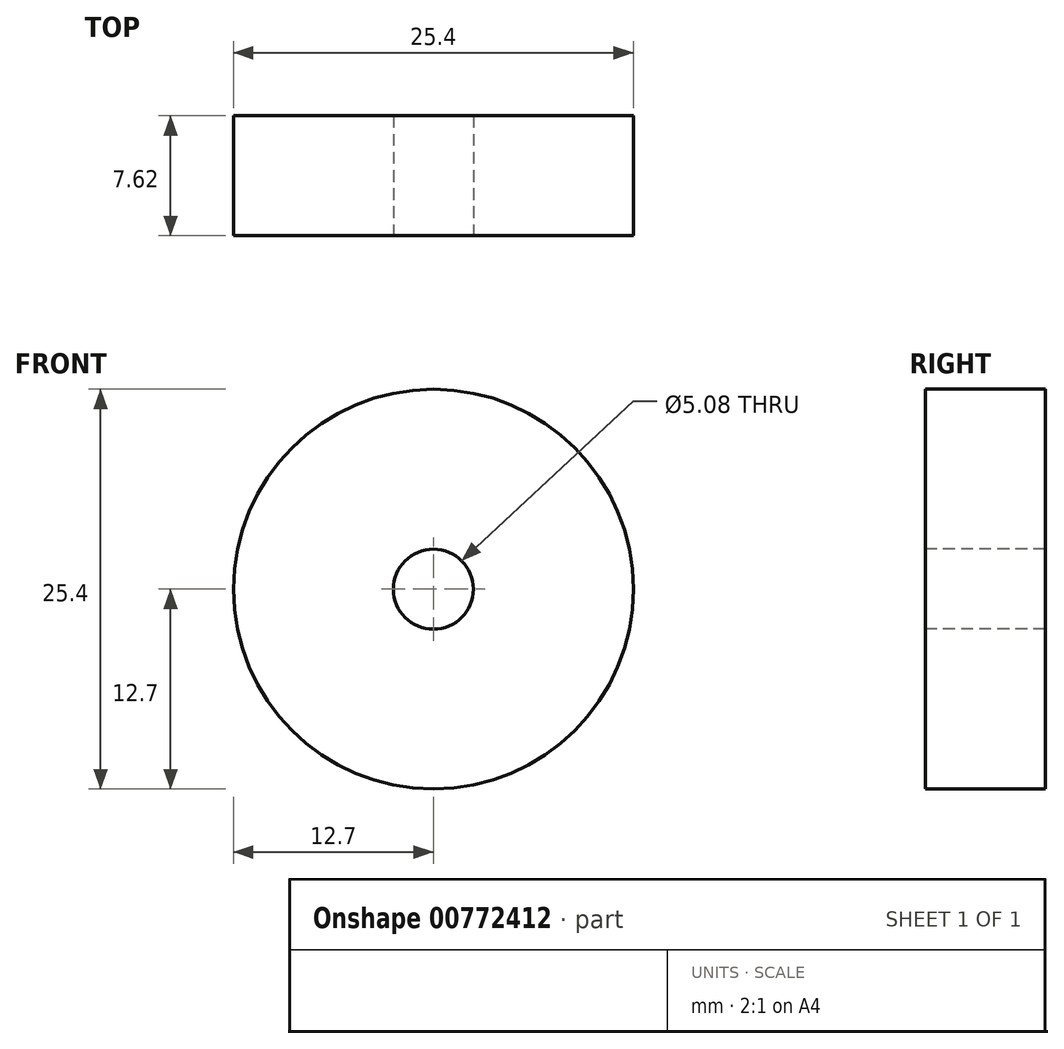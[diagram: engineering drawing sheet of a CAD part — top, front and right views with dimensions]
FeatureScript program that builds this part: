
annotation { "Feature Type Name" : "Feature", "Feature Type Description" : "" }
export const myFeature = defineFeature(function(context is Context, id is Id, definition is map)
    precondition{}
    {
        {
            var Q0;
            Q0=qCreatedBy(makeId("Front.planeOp"),FACE);
            var sketch = newSketch(context, id + "F0", { "sketchPlane" : qUnion([Q0])});
            skCircle(sketch, "E0", {"center": v(0, 0) * mm, "radius": 12.7 * mm});
            skCircle(sketch, "E1", {"center": v(0, 0) * mm, "radius": 2.54 * mm});
            skSolve(sketch);
        }
        {
            var Q0;
            Q0 = qSketchRegion(id + "F0", true);
            extrude(context, id + "F1", {"entities" : qUnion([Q0]), "endBound" : BoundingType.SYMMETRIC, "oppositeDirection" : true, "depth" : 7.62 * mm, "offsetDistance" : 25.4 * mm});
        }
    });
